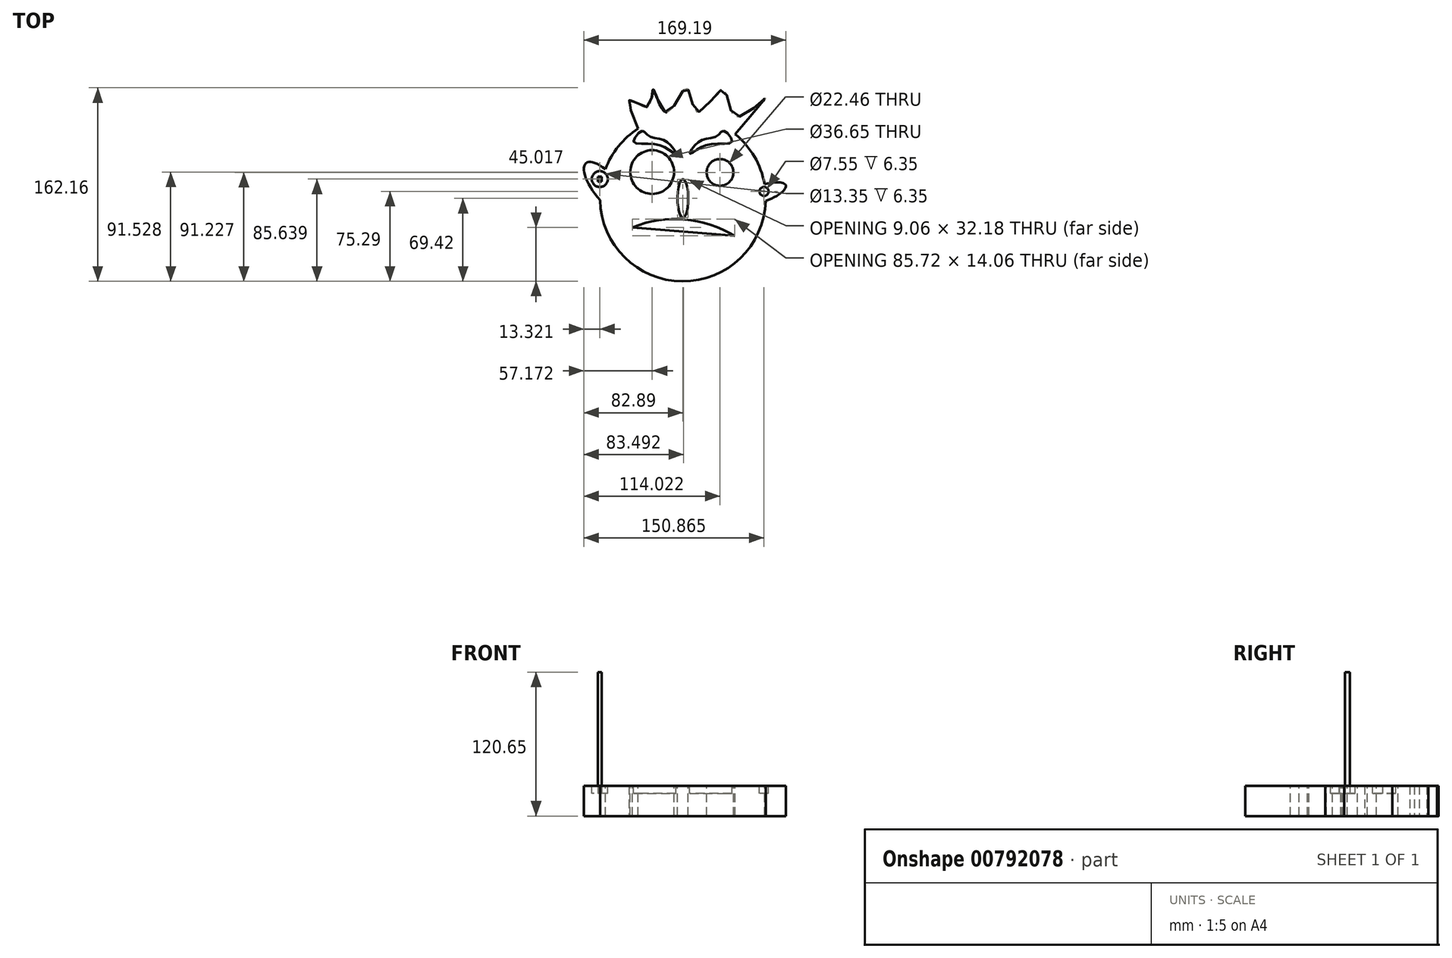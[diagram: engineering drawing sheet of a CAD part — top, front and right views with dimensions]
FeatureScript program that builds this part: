
annotation { "Feature Type Name" : "Feature", "Feature Type Description" : "" }
export const myFeature = defineFeature(function(context is Context, id is Id, definition is map)
    precondition{}
    {
        {
            var Q0;
            Q0=qCreatedBy(makeId("Top.planeOp"),FACE);
            var sketch = newSketch(context, id + "F0", { "sketchPlane" : qUnion([Q0])});
            skCircle(sketch, "E0", {"center": v(0, 0) * mm, "radius": 69.42 * mm});
            skSolve(sketch);
        }
        {
            var Q0;
            Q0 = qSketchRegion(id + "F0", true);
            extrude(context, id + "F1", {"entities" : qUnion([Q0]), "depth" : 25.4 * mm, "offsetDistance" : 25.4 * mm});
        }
        {
            var Q0;
            Q0=makeQuery(id+"F1.opExtrude","CAP_FACE",FACE,{"disambiguationData":[OSD([sQuery(id+"F0.wireOp",EDGE,"E0")])],"isStart":false});
            var sketch = newSketch(context, id + "F2", { "sketchPlane" : qUnion([Q0])});
            skCircle(sketch, "E1", {"center": v(-25.72, 22.1) * mm, "radius": 18.33 * mm});
            skCircle(sketch, "E2", {"center": v(31.13, 21.8) * mm, "radius": 11.23 * mm});
            skEllipse(sketch, "E3", {"center": v(0, 0) * mm, "majorRadius": 16.1 * mm, "minorRadius": 4.53 * mm, "majorAxis": v(0, -1)});
            skSolve(sketch);
        }
        {
            var Q0;
            Q0 = qSketchRegion(id + "F2", true);
            extrude(context, id + "F3", {"entities" : qUnion([Q0]), "operationType" : NewBodyOperationType.REMOVE, "oppositeDirection" : true, "depth" : 25.4 * mm, "offsetDistance" : 25.4 * mm});
        }
        {
            var Q0;
            Q0=makeQuery(id+"F1.opExtrude","CAP_FACE",FACE,{"disambiguationData":[OSD([sQuery(id+"F0.wireOp",EDGE,"E0")])],"isStart":false});
            var sketch = newSketch(context, id + "F4", { "sketchPlane" : qUnion([Q0])});
            skArc(sketch, "E4", {"start": v(43.46, -31.43) * mm, "mid": v(1.46, -17.66) * mm, "end": v(-42.26, -24.21) * mm});
            skLineSegment(sketch, "E5", {"start": v(-42.26, -24.21) * mm, "end": v(43.46, -31.43) * mm});
            skSolve(sketch);
        }
        {
            var Q0;
            Q0 = qSketchRegion(id + "F4", true);
            extrude(context, id + "F5", {"entities" : qUnion([Q0]), "operationType" : NewBodyOperationType.REMOVE, "oppositeDirection" : true, "depth" : 25.4 * mm, "offsetDistance" : 25.4 * mm});
        }
        {
            var Q0;
            Q0=makeQuery(id+"F1.opExtrude","CAP_FACE",FACE,{"disambiguationData":[OSD([sQuery(id+"F0.wireOp",EDGE,"E0")])],"isStart":false});
            var sketch = newSketch(context, id + "F6", { "sketchPlane" : qUnion([Q0])});
            skEllipse(sketch, "E6", {"center": v(65.42, 3.76) * mm, "majorRadius": 21.97 * mm, "minorRadius": 6.93 * mm, "majorAxis": v(0.94, 0.33)});
            skEllipse(sketch, "E7", {"center": v(-63.32, 7.97) * mm, "majorRadius": 28 * mm, "minorRadius": 10.67 * mm, "majorAxis": v(-0.63, 0.77)});
            skSolve(sketch);
        }
        {
            var Q0;
            Q0 = qSketchRegion(id + "F6", true);
            extrude(context, id + "F7", {"entities" : qUnion([Q0]), "operationType" : NewBodyOperationType.ADD, "oppositeDirection" : true, "depth" : 25.4 * mm, "offsetDistance" : 25.4 * mm});
        }
        {
            var Q0;
            Q0=makeQuery(id+"F7.boolean.opBoolean","MERGE",FACE,{"derivedFrom":[makeQuery(id+"F1.opExtrude","CAP_FACE",FACE,{"disambiguationData":[OSD([sQuery(id+"F0.wireOp",EDGE,"E0")])],"isStart":false}),makeQuery(id+"F7.opExtrude","CAP_FACE",FACE,{"disambiguationData":[OSD([sQuery(id+"F6.wireOp",EDGE,"E6")])],"isStart":true}),makeQuery(id+"F7.opExtrude","CAP_FACE",FACE,{"disambiguationData":[OSD([sQuery(id+"F6.wireOp",EDGE,"E7")])],"isStart":true})]});
            var sketch = newSketch(context, id + "F8", { "sketchPlane" : qUnion([Q0])});
            skFitSpline(sketch, "E8", {"points": [v(-34.71, 52.29) * mm, v(-43.9, 82.8) * mm, v(-29.2, 76.92) * mm, v(-24.79, 91.26) * mm, v(-13.76, 72.14) * mm, v(3.16, 92.73) * mm, v(11.98, 72.5) * mm, v(33.67, 91.26) * mm, v(43.96, 68.83) * mm, v(68.6, 83.9) * mm, v(37.71, 46.77) * mm], "startDerivative": vector(-178.06, 415.4) * mm, "endDerivative": vector(-376.2, -437.84) * mm});
            skLineSegment(sketch, "E9", {"start": v(-34.71, 52.29) * mm, "end": v(37.71, 46.77) * mm});
            skSolve(sketch);
        }
        {
            var Q0;
            Q0 = qSketchRegion(id + "F8", true);
            extrude(context, id + "F9", {"entities" : qUnion([Q0]), "operationType" : NewBodyOperationType.ADD, "oppositeDirection" : true, "depth" : 25.4 * mm, "offsetDistance" : 25.4 * mm});
        }
        {
            var Q0;
            Q0=makeQuery(id+"F9.boolean.opBoolean","MERGE",FACE,{"derivedFrom":[makeQuery(id+"F7.boolean.opBoolean","MERGE",FACE,{"derivedFrom":[makeQuery(id+"F1.opExtrude","CAP_FACE",FACE,{"disambiguationData":[OSD([sQuery(id+"F0.wireOp",EDGE,"E0")])],"isStart":false}),makeQuery(id+"F7.opExtrude","CAP_FACE",FACE,{"disambiguationData":[OSD([sQuery(id+"F6.wireOp",EDGE,"E6")])],"isStart":true}),makeQuery(id+"F7.opExtrude","CAP_FACE",FACE,{"disambiguationData":[OSD([sQuery(id+"F6.wireOp",EDGE,"E7")])],"isStart":true})]}),makeQuery(id+"F9.opExtrude","CAP_FACE",FACE,{"disambiguationData":[OSD([sQuery(id+"F8.wireOp",EDGE,"E8"),sQuery(id+"F8.wireOp",EDGE,"E9")])],"isStart":true})]});
            var sketch = newSketch(context, id + "F10", { "sketchPlane" : qUnion([Q0])});
            skCircle(sketch, "E10", {"center": v(-69.57, 16.22) * mm, "radius": 6.68 * mm});
            skCircle(sketch, "E11", {"center": v(67.98, 5.87) * mm, "radius": 3.78 * mm});
            skSolve(sketch);
        }
        {
            var Q0;
            Q0 = qSketchRegion(id + "F10", true);
            extrude(context, id + "F11", {"entities" : qUnion([Q0]), "operationType" : NewBodyOperationType.REMOVE, "oppositeDirection" : true, "depth" : 6.35 * mm, "offsetDistance" : 25.4 * mm});
        }
        {
            var Q0;
            Q0=makeQuery(id+"F11.boolean.opBoolean","COPY",FACE,{"derivedFrom":makeQuery(id+"F11.opExtrude","CAP_FACE",FACE,{"disambiguationData":[OSD([sQuery(id+"F10.wireOp",EDGE,"E10")])],"isStart":false})});
            var sketch = newSketch(context, id + "F12", { "sketchPlane" : qUnion([Q0])});
            skLineSegment(sketch, "E12.bottom", {"start": v(-68.06, 14.05) * mm, "end": v(-71.07, 14.05) * mm});
            skLineSegment(sketch, "E12.top", {"start": v(-68.06, 18.39) * mm, "end": v(-71.07, 18.39) * mm});
            skLineSegment(sketch, "E12.left", {"start": v(-68.06, 14.05) * mm, "end": v(-68.06, 18.39) * mm});
            skLineSegment(sketch, "E12.right", {"start": v(-71.07, 14.05) * mm, "end": v(-71.07, 18.39) * mm});
            skPoint(sketch, "E12.middle", {"position": v(-69.57, 16.22) * mm});
            skSolve(sketch);
        }
        {
            var Q0;
            Q0 = qSketchRegion(id + "F12", true);
            extrude(context, id + "F13", {"entities" : qUnion([Q0]), "operationType" : NewBodyOperationType.ADD, "depth" : 101.6 * mm, "offsetDistance" : 25.4 * mm});
        }
        {
            var Q0;
            Q0=makeQuery(id+"F9.boolean.opBoolean","MERGE",FACE,{"derivedFrom":[makeQuery(id+"F7.boolean.opBoolean","MERGE",FACE,{"derivedFrom":[makeQuery(id+"F1.opExtrude","CAP_FACE",FACE,{"disambiguationData":[OSD([sQuery(id+"F0.wireOp",EDGE,"E0")])],"isStart":false}),makeQuery(id+"F7.opExtrude","CAP_FACE",FACE,{"disambiguationData":[OSD([sQuery(id+"F6.wireOp",EDGE,"E6")])],"isStart":true}),makeQuery(id+"F7.opExtrude","CAP_FACE",FACE,{"disambiguationData":[OSD([sQuery(id+"F6.wireOp",EDGE,"E7")])],"isStart":true})]}),makeQuery(id+"F9.opExtrude","CAP_FACE",FACE,{"disambiguationData":[OSD([sQuery(id+"F8.wireOp",EDGE,"E8"),sQuery(id+"F8.wireOp",EDGE,"E9")])],"isStart":true})]});
            var sketch = newSketch(context, id + "F14", { "sketchPlane" : qUnion([Q0])});
            skFitSpline(sketch, "E13", {"points": [v(-34.18, 56.61) * mm, v(-41.2, 47.6) * mm, v(-26.5, 45.93) * mm, v(-11.48, 40.6) * mm, v(-5.8, 37.59) * mm, v(-9.81, 44.26) * mm, v(-19.16, 49.94) * mm, v(-29.5, 52.94) * mm, v(-34.18, 56.61) * mm]});
            skFitSpline(sketch, "E14.MirrorC", {"points": [v(34.18, 56.61) * mm, v(41.2, 47.6) * mm, v(26.5, 45.93) * mm, v(11.48, 40.6) * mm, v(5.8, 37.59) * mm, v(9.81, 44.26) * mm, v(19.16, 49.94) * mm, v(29.5, 52.94) * mm, v(34.18, 56.61) * mm]});
            skSolve(sketch);
        }
        {
            var Q0;
            Q0 = qSketchRegion(id + "F14", true);
            extrude(context, id + "F15", {"entities" : qUnion([Q0]), "operationType" : NewBodyOperationType.REMOVE, "oppositeDirection" : true, "depth" : 6.35 * mm, "offsetDistance" : 25.4 * mm});
        }
    });
